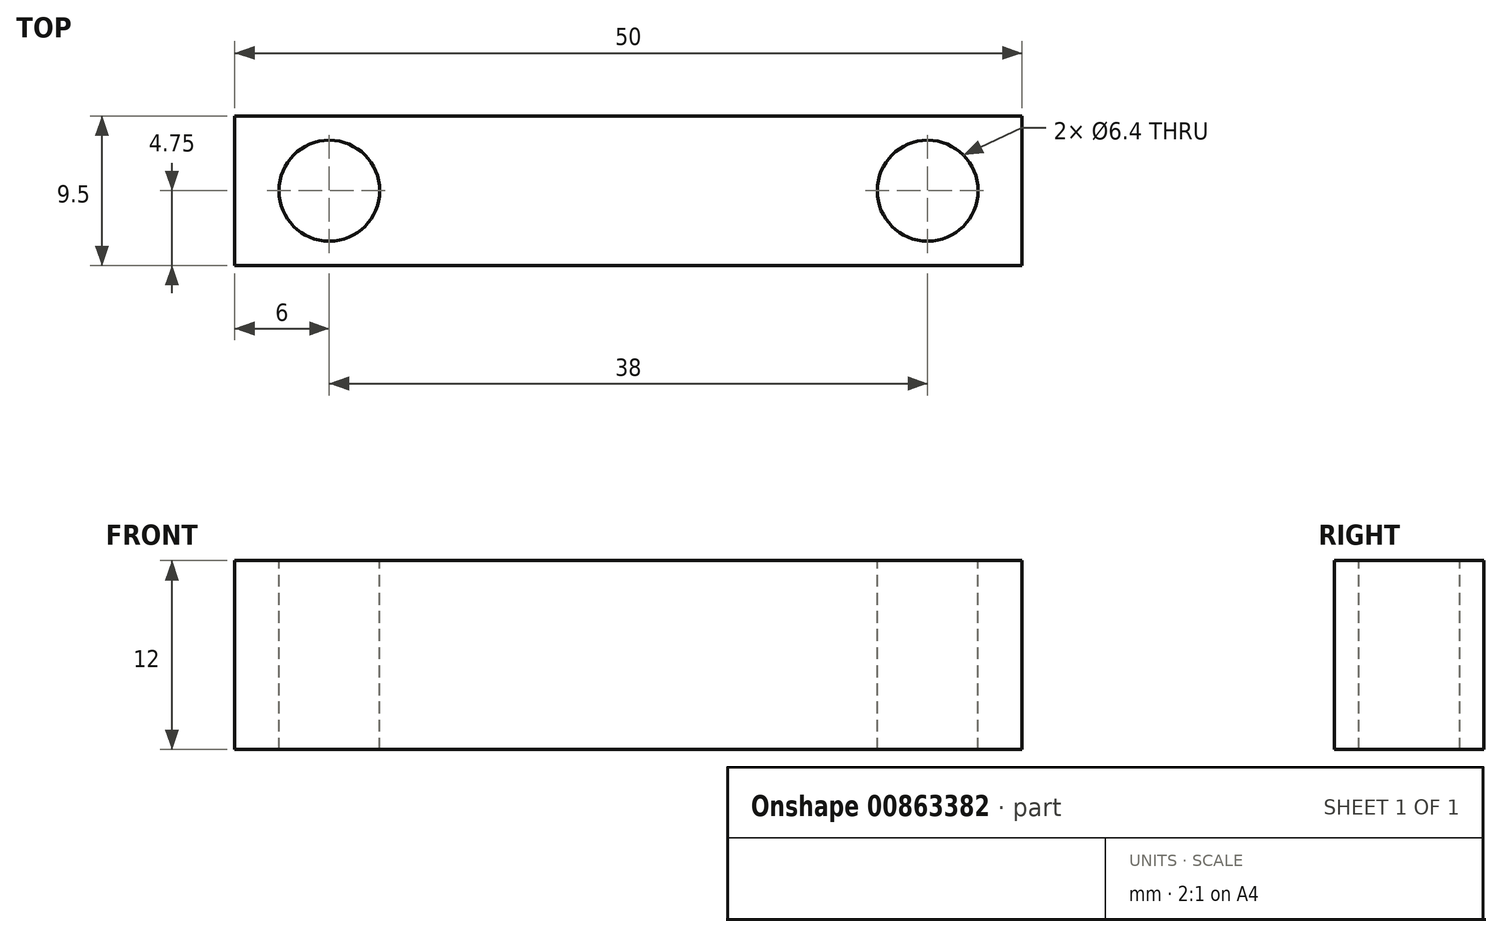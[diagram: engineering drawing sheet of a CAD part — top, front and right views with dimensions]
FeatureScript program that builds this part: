
annotation { "Feature Type Name" : "Feature", "Feature Type Description" : "" }
export const myFeature = defineFeature(function(context is Context, id is Id, definition is map)
    precondition{}
    {
        {
            var Q0;
            Q0=qCreatedBy(makeId("Top.planeOp"),FACE);
            var sketch = newSketch(context, id + "F0", { "sketchPlane" : qUnion([Q0])});
            skLineSegment(sketch, "E0.bottom", {"start": v(25, -4.75) * mm, "end": v(-25, -4.75) * mm});
            skLineSegment(sketch, "E0.top", {"start": v(25, 4.75) * mm, "end": v(-25, 4.75) * mm});
            skLineSegment(sketch, "E0.left", {"start": v(25, -4.75) * mm, "end": v(25, 4.75) * mm});
            skLineSegment(sketch, "E0.right", {"start": v(-25, -4.75) * mm, "end": v(-25, 4.75) * mm});
            skPoint(sketch, "E0.middle", {"position": v(0, 0) * mm});
            skSolve(sketch);
        }
        {
            var Q0;
            Q0 = qSketchRegion(id + "F0", true);
            extrude(context, id + "F1", {"entities" : qUnion([Q0]), "depth" : 12 * mm, "offsetDistance" : 25 * mm});
        }
        {
            var Q0;
            Q0=makeQuery(id+"F1.opExtrude","CAP_FACE",FACE,{"disambiguationData":[OSD([sQuery(id+"F0.wireOp",EDGE,"E0.bottom"),sQuery(id+"F0.wireOp",EDGE,"E0.top"),sQuery(id+"F0.wireOp",EDGE,"E0.left"),sQuery(id+"F0.wireOp",EDGE,"E0.right")])],"isStart":false});
            var sketch = newSketch(context, id + "F2", { "sketchPlane" : qUnion([Q0])});
            skPoint(sketch, "E1", {"position": v(-19, 0) * mm});
            skPoint(sketch, "E2", {"position": v(19, 0) * mm});
            skCircle(sketch, "E3", {"center": v(-19, 0) * mm, "radius": 3.2 * mm});
            skCircle(sketch, "E4", {"center": v(19, 0) * mm, "radius": 3.2 * mm});
            skSolve(sketch);
        }
        {
            var Q0;
            Q0 = qSketchRegion(id + "F2", true);
            extrude(context, id + "F3", {"entities" : qUnion([Q0]), "operationType" : NewBodyOperationType.REMOVE, "endBound" : BoundingType.THROUGH_ALL, "oppositeDirection" : true, "depth" : 25 * mm, "offsetDistance" : 25 * mm});
        }
    });
